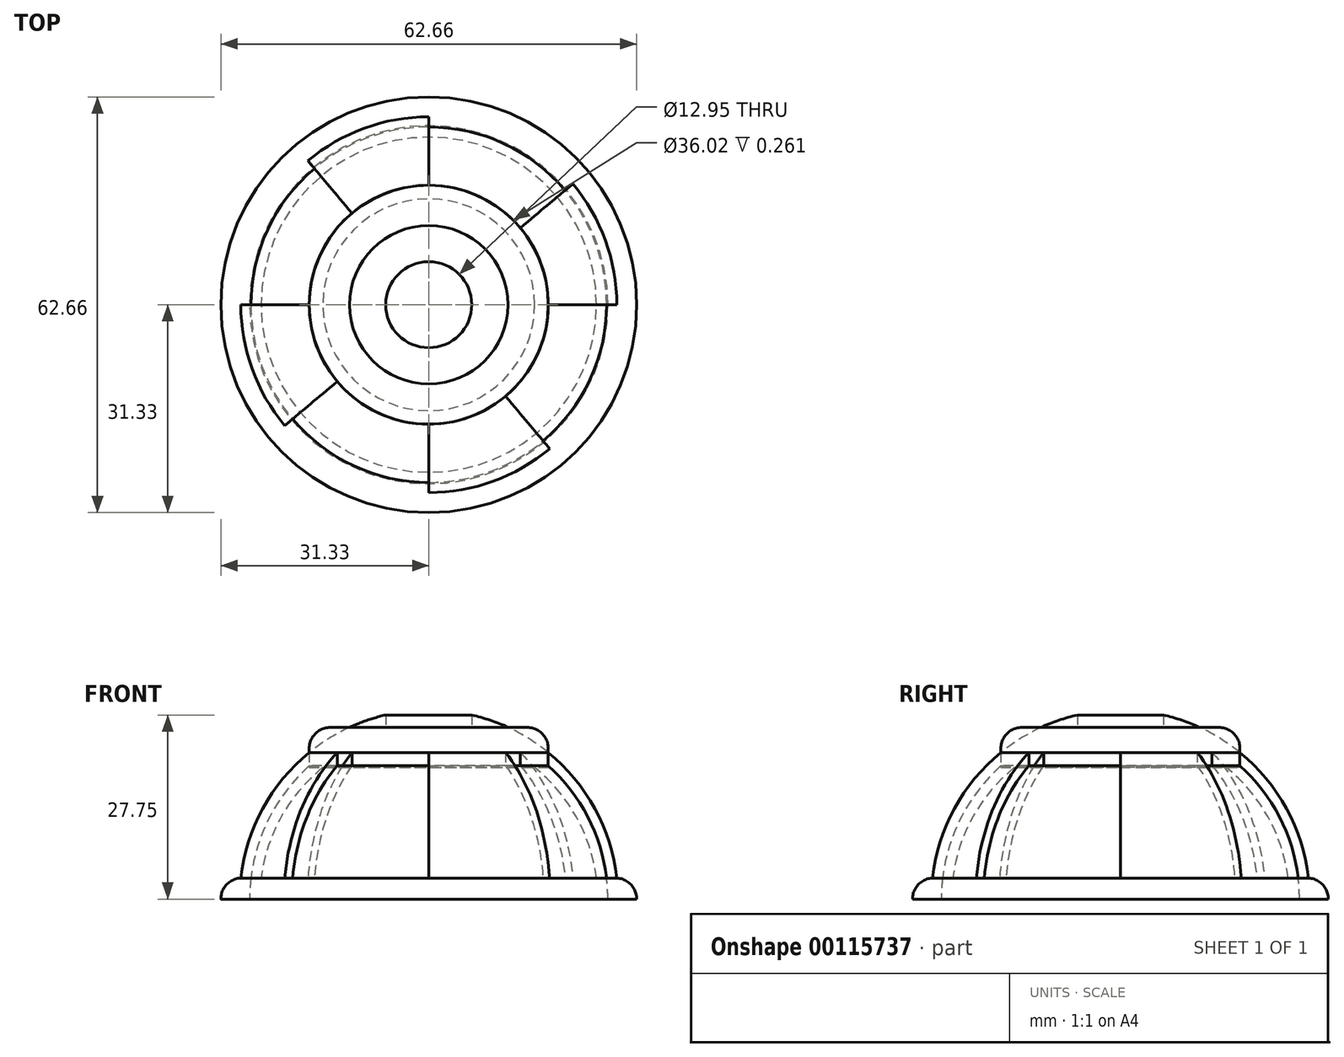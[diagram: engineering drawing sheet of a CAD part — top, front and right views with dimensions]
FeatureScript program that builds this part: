
annotation { "Feature Type Name" : "Feature", "Feature Type Description" : "" }
export const myFeature = defineFeature(function(context is Context, id is Id, definition is map)
    precondition{}
    {
        {
            var Q0;
            Q0=qCreatedBy(makeId("Front.planeOp"),FACE);
            var sketch = newSketch(context, id + "F0", { "sketchPlane" : qUnion([Q0])});
            skCircle(sketch, "E0", {"center": v(0, 0) * mm, "radius": 28.5 * mm});
            skCircle(sketch, "E1", {"center": v(0, 0) * mm, "radius": 26.98 * mm});
            skLineSegment(sketch, "E2.bottom", {"start": v(-28.15, 3.18) * mm, "end": v(28.15, 3.18) * mm});
            skLineSegment(sketch, "E2.top", {"start": v(-31.33, -3.18) * mm, "end": v(31.33, -3.18) * mm});
            skLineSegment(sketch, "E2.left", {"start": v(-31.33, 0) * mm, "end": v(-31.33, -3.18) * mm});
            skLineSegment(sketch, "E2.right", {"start": v(31.33, 0) * mm, "end": v(31.33, -3.18) * mm});
            skLineSegment(sketch, "E3", {"start": v(-31.33, 0) * mm, "end": v(0, 0) * mm});
            skLineSegment(sketch, "E4", {"start": v(0, 0) * mm, "end": v(0, 28.5) * mm});
            skLineSegment(sketch, "E5.bottom", {"start": v(-14.83, 25.88) * mm, "end": v(14.83, 25.88) * mm});
            skLineSegment(sketch, "E5.top", {"start": v(-18, 19.82) * mm, "end": v(18, 19.82) * mm});
            skLineSegment(sketch, "E5.left", {"start": v(-18, 22.7) * mm, "end": v(-18, 19.82) * mm});
            skLineSegment(sketch, "E5.right", {"start": v(18, 22.7) * mm, "end": v(18, 19.82) * mm});
            skPoint(sketch, "E5.middle", {"position": v(0, 22.85) * mm});
            skPoint(sketch, "E6.visualSharp", {"position": v(-18, 25.88) * mm});
            skArc(sketch, "E6.filletArc", {"start": v(-14.83, 25.88) * mm, "mid": v(-17.08, 24.95) * mm, "end": v(-18, 22.7) * mm});
            skPoint(sketch, "E7.visualSharp", {"position": v(18, 25.88) * mm});
            skArc(sketch, "E7.filletArc", {"start": v(18, 22.7) * mm, "mid": v(17.08, 24.95) * mm, "end": v(14.83, 25.88) * mm});
            skPoint(sketch, "E8.visualSharp", {"position": v(-31.33, 3.18) * mm});
            skArc(sketch, "E8.filletArc", {"start": v(-28.15, 3.18) * mm, "mid": v(-30.4, 2.25) * mm, "end": v(-31.33, 0) * mm});
            skPoint(sketch, "E9.visualSharp", {"position": v(31.33, 3.18) * mm});
            skArc(sketch, "E9.filletArc", {"start": v(31.33, 0) * mm, "mid": v(30.4, 2.25) * mm, "end": v(28.15, 3.18) * mm});
            skCircle(sketch, "E10", {"center": v(0, 0) * mm, "radius": 25.45 * mm});
            skSolve(sketch);
        }
        {
            var Q0;
            {var subQ5=sQuery(id+"F0.wireOp",EDGE,"E5.bottom");var subQ6=sQuery(id+"F0.wireOp",EDGE,"E1");var subQ7=makeQuery(id+"F0.imprint","INTERSECT",VERTEX,{"disambiguationData":[OD(1.0)],"derivedFrom":[subQ6,subQ5]});Q0=makeQuery(id+"F0.imprint","IMPRINT",FACE,{"disambiguationData":[TD([[makeQuery(id+"F0.imprint","IMPRINT",EDGE,{"disambiguationData":[TD([[subQ7,-1.0]])],"derivedFrom":subQ6}),1.0]])]});}
            var Q1;
            {var subQ0=sQuery(id+"F0.wireOp",EDGE,"E5.bottom");var subQ1=sQuery(id+"F0.wireOp",EDGE,"E0");var subQ2=makeQuery(id+"F0.imprint","INTERSECT",VERTEX,{"disambiguationData":[OD(1.0)],"derivedFrom":[subQ1,subQ0]});Q1=makeQuery(id+"F0.imprint","IMPRINT",FACE,{"disambiguationData":[TD([[makeQuery(id+"F0.imprint","IMPRINT",EDGE,{"disambiguationData":[TD([[subQ2,-1.0]])],"derivedFrom":subQ1}),1.0]])]});}
            var Q2;
            {var subQ5=sQuery(id+"F0.wireOp",EDGE,"E6.filletArc");Q2=makeQuery(id+"F0.imprint","IMPRINT",FACE,{"disambiguationData":[TD([[makeQuery(id+"F0.imprint","IMPRINT",EDGE,{"derivedFrom":subQ5}),1.0]])]});}
            var Q3;
            {var subQ0=sQuery(id+"F0.wireOp",EDGE,"E5.left");var subQ6=sQuery(id+"F0.wireOp",EDGE,"E1");var subQ9=makeQuery(id+"F0.imprint","INTERSECT",VERTEX,{"derivedFrom":[subQ6,subQ0]});Q3=makeQuery(id+"F0.imprint","IMPRINT",FACE,{"disambiguationData":[TD([[makeQuery(id+"F0.imprint","IMPRINT",EDGE,{"disambiguationData":[TD([[subQ9,-1.0]])],"derivedFrom":subQ6}),1.0]])]});}
            var Q4;
            {var subQ0=sQuery(id+"F0.wireOp",EDGE,"E2.bottom");var subQ1=sQuery(id+"F0.wireOp",EDGE,"E1");var subQ2=makeQuery(id+"F0.imprint","INTERSECT",VERTEX,{"disambiguationData":[OD(1.0)],"derivedFrom":[subQ1,subQ0]});Q4=makeQuery(id+"F0.imprint","IMPRINT",FACE,{"disambiguationData":[TD([[makeQuery(id+"F0.imprint","IMPRINT",EDGE,{"disambiguationData":[TD([[subQ2,-1.0]])],"derivedFrom":subQ1}),1.0]])]});}
            var Q5;
            {var subQ5=sQuery(id+"F0.wireOp",EDGE,"E0");var subQ7=sQuery(id+"F0.wireOp",EDGE,"E8.filletArc");var subQ8=makeQuery(id+"F0.imprint","INTERSECT",VERTEX,{"derivedFrom":[subQ5,subQ7]});Q5=makeQuery(id+"F0.imprint","IMPRINT",FACE,{"disambiguationData":[TD([[makeQuery(id+"F0.imprint","IMPRINT",EDGE,{"disambiguationData":[TD([[subQ8,-1.0]])],"derivedFrom":subQ5}),1.0]])]});}
            var Q6;
            {var subQ0=sQuery(id+"F0.wireOp",EDGE,"E8.filletArc");var subQ1=sQuery(id+"F0.wireOp",EDGE,"E0");var subQ2=makeQuery(id+"F0.imprint","INTERSECT",VERTEX,{"derivedFrom":[subQ1,subQ0]});Q6=makeQuery(id+"F0.imprint","IMPRINT",FACE,{"disambiguationData":[TD([[makeQuery(id+"F0.imprint","IMPRINT",EDGE,{"disambiguationData":[TD([[subQ2,-1.0]])],"derivedFrom":subQ1}),-1.0]])]});}
            var Q7;
            Q7=sQuery(id+"F0.wireOp",EDGE,"E4");
            revolve(context, id + "F1", {"entities" : qUnion([Q0, Q1, Q2, Q3, Q4, Q5, Q6]), "axis" : qUnion([Q7]), "revolveType" : RevolveType.FULL});
        }
        {
            var Q0;
            {var subQ0=sQuery(id+"F0.wireOp",EDGE,"E5.left");var subQ1=sQuery(id+"F0.wireOp",EDGE,"E0");var subQ2=makeQuery(id+"F0.imprint","INTERSECT",VERTEX,{"derivedFrom":[subQ1,subQ0]});Q0=makeQuery(id+"F0.imprint","IMPRINT",FACE,{"disambiguationData":[TD([[makeQuery(id+"F0.imprint","IMPRINT",EDGE,{"disambiguationData":[TD([[subQ2,-1.0]])],"derivedFrom":subQ1}),1.0]])]});}
            var Q1;
            Q1=sQuery(id+"F0.wireOp",EDGE,"E4");
            revolve(context, id + "F2", {"operationType" : NewBodyOperationType.ADD, "entities" : qUnion([Q0]), "axis" : qUnion([Q1]), "revolveType" : RevolveType.ONE_DIRECTION, "angle" : 40 * degree});
        }
        {
            var Q0;
            Q0=makeQuery(id+"F1.opRevolve","SWEPT_BODY",BODY,{"disambiguationData":[OSD([sQuery(id+"F0.wireOp",EDGE,"E1"),sQuery(id+"F0.wireOp",EDGE,"E2.bottom"),sQuery(id+"F0.wireOp",EDGE,"E2.left"),sQuery(id+"F0.wireOp",EDGE,"E3"),sQuery(id+"F0.wireOp",EDGE,"E4"),sQuery(id+"F0.wireOp",EDGE,"E5.bottom"),sQuery(id+"F0.wireOp",EDGE,"E5.left"),sQuery(id+"F0.wireOp",EDGE,"E6.filletArc"),sQuery(id+"F0.wireOp",EDGE,"E8.filletArc"),sQuery(id+"F0.wireOp",EDGE,"E10")])]});
            var Q1;
            Q1=sQuery(id+"F0.wireOp",EDGE,"E4");
            circularPattern(context, id + "F3", {"operationType" : NewBodyOperationType.ADD, "entities" : qUnion([Q0]), "axis" : qUnion([Q1]), "angle" : 360 * degree, "instanceCount" : 4, "equalSpace" : true});
        }
        {
            var Q0;
            Q0=makeQuery(id+"F1.opRevolve","SWEPT_FACE",FACE,{"disambiguationData":[OSD([sQuery(id+"F0.wireOp",EDGE,"E5.bottom")])]});
            var sketch = newSketch(context, id + "F4", { "sketchPlane" : qUnion([Q0])});
            skCircle(sketch, "E11", {"center": v(0, 0) * mm, "radius": 6.48 * mm});
            skSolve(sketch);
        }
        {
            var Q0;
            Q0=makeQuery(id+"F4.imprint","IMPRINT",FACE,{"disambiguationData":[TD([[makeQuery(id+"F4.imprint","IMPRINT",EDGE,{"derivedFrom":sQuery(id+"F4.wireOp",EDGE,"E11")}),1.0]])]});
            extrude(context, id + "F5", {"entities" : qUnion([Q0]), "operationType" : NewBodyOperationType.REMOVE, "oppositeDirection" : true, "depth" : 25.4 * mm});
        }
    });
